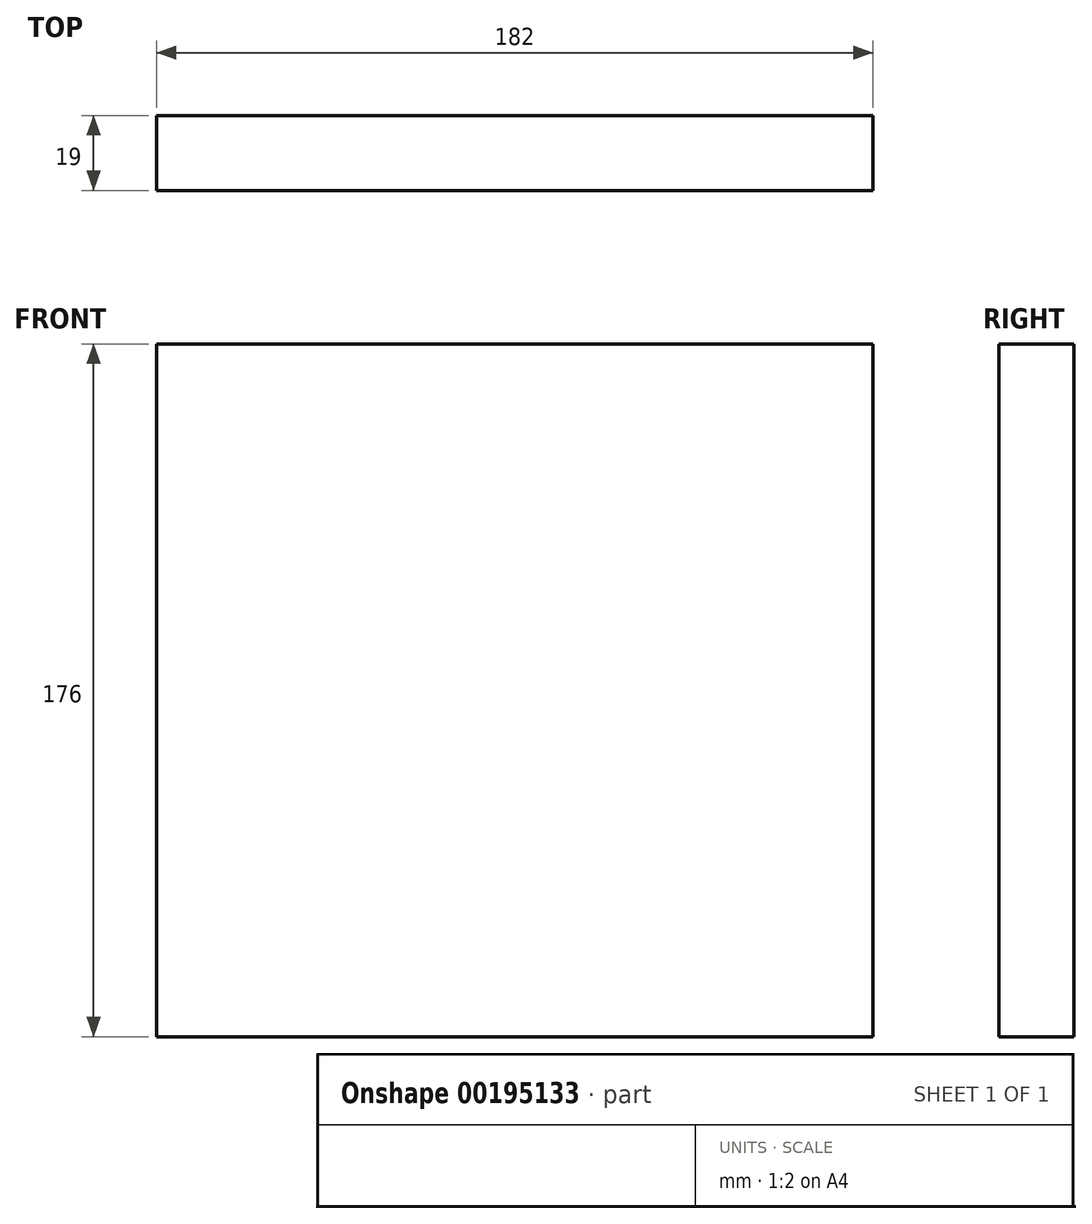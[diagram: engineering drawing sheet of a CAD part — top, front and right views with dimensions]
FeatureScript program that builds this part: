
annotation { "Feature Type Name" : "Feature", "Feature Type Description" : "" }
export const myFeature = defineFeature(function(context is Context, id is Id, definition is map)
    precondition{}
    {
        {
            var Q0;
            Q0=qCreatedBy(makeId("Front.planeOp"),FACE);
            var sketch = newSketch(context, id + "F0", { "sketchPlane" : qUnion([Q0])});
            skLineSegment(sketch, "E0.bottom", {"start": v(-91.16, 37.29) * mm, "end": v(90.84, 37.29) * mm});
            skLineSegment(sketch, "E0.top", {"start": v(-91.16, -138.71) * mm, "end": v(90.84, -138.71) * mm});
            skLineSegment(sketch, "E0.left", {"start": v(-91.16, 37.29) * mm, "end": v(-91.16, -138.71) * mm});
            skLineSegment(sketch, "E0.right", {"start": v(90.84, 37.29) * mm, "end": v(90.84, -138.71) * mm});
            skSolve(sketch);
        }
        {
            var Q0;
            Q0=makeQuery(id+"F0.imprint","IMPRINT",FACE,{"disambiguationData":[TD([[makeQuery(id+"F0.imprint","IMPRINT",EDGE,{"derivedFrom":sQuery(id+"F0.wireOp",EDGE,"E0.bottom")}),-1.0]])]});
            extrude(context, id + "F1", {"entities" : qUnion([Q0]), "depth" : 19 * mm});
        }
    });
